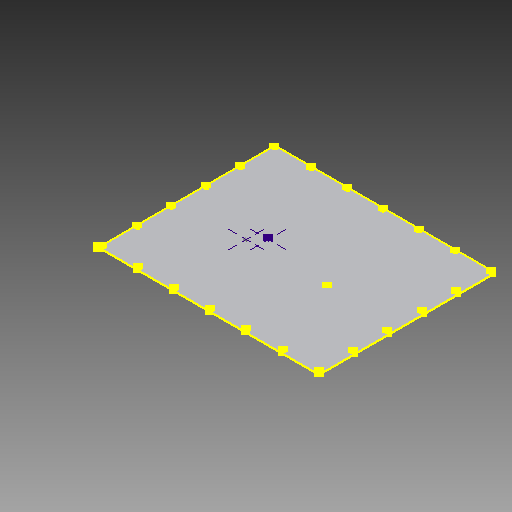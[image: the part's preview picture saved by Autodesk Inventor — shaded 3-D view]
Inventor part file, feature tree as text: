
AUTODESK INVENTOR PART (.ipt)
format: ipt  version: 2017 (Build 210142000, 142)  size: 189,440 bytes
history: native  units: in
note: dims shown in document units (in); Inventor stores cm internally (conversion verified against a paired STEP export)
features: sketch x5, hole x4, pattern_linear x4, extrude x1
ambient origin geometry x8: Origin, YZ Plane, XZ Plane, XY Plane, X Axis, Y Axis, Z Axis, Center Point
bodies: Solid1 (feature_tree)
feature tree (14):
  extrude  "Extrusion1"  Depth=8.0in
  sketch  "Sketch2"  dims[d4=0.06in d5=0.0in]
  hole  "Hole1"  [1 undecoded]
  pattern_linear  "Rectangular Pattern1"  Count1=7 Spacing1=1.635in
  pattern_linear  "Rectangular Pattern2"  Count1=5 Spacing1=1.562in
  hole  "Hole2"  [1 undecoded]
  pattern_linear  "Rectangular Pattern3"  Count1=5 Spacing1=1.562in
  pattern_linear  "Rectangular Pattern4"  Count1=7 Spacing1=1.635in
  sketch  "Sketch3"  dims[d6=0.096in d7=0.75in d8=0.16in d9=0.25in d10=0.5635in d11=1.0in d12=0.8108in d13=0.0935in]
  sketch  "Sketch6"  dims[d14=0.0935in d15=2.7559in d17=1.635in d18=1.9685in d20=1.562in]
  sketch  "Sketch7"  dims[d21=0.0935in d22=0.0935in d23=0.096in d24=0.75in d25=0.16in d26=0.25in d27=0.5635in d28=1.0in d29=0.8108in d30=1.9685in d32=1.562in d33=2.7559in d35=1.635in d36=0.128in d37=0.75in d38=0.232in d39=0.25in d40=0.5635in d41=0.06in d42=0.8108in d43=0.128in d44=0.75in d45=0.232in d46=0.25in d47=0.5635in d48=1.0in d49=0.8108in d50=3.656in d51=4.156in d52=3.062in d53=3.562in]
  hole  "Hole3"  [1 undecoded]
  hole  "Hole4"  [1 undecoded]
  sketch  "Sketch1"  dims[d0=10.0in d3=8.0in]
note: 4 required parameter values undecoded (feature->parameter linkage not recoverable at this tier; creation-order binding heuristic only, values carry confidence <= 0.55)
